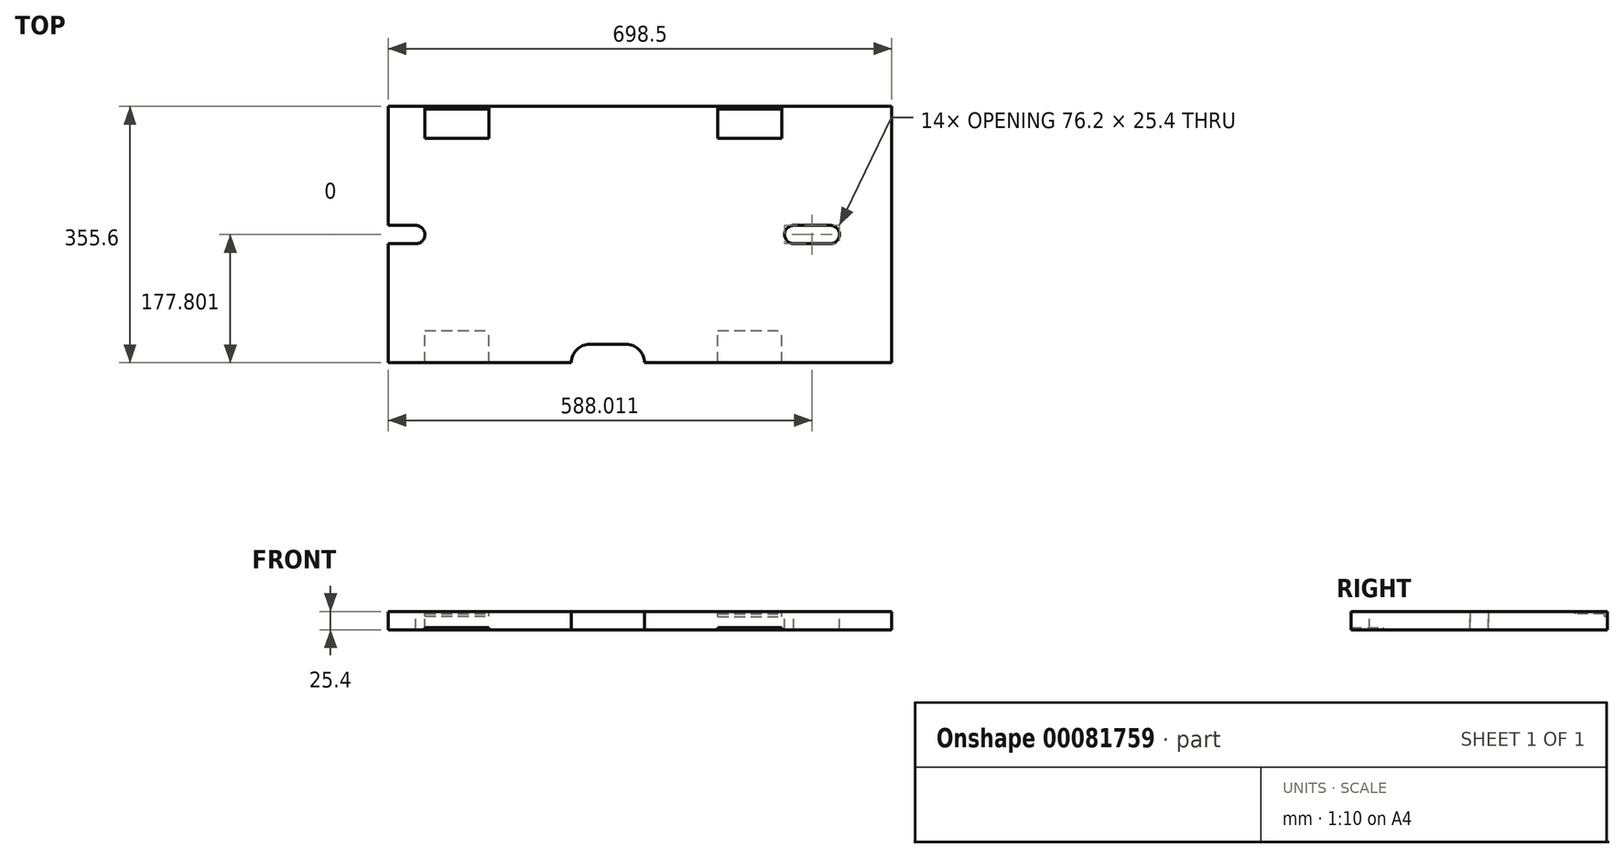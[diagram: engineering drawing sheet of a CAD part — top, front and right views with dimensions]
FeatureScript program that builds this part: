
annotation { "Feature Type Name" : "Feature", "Feature Type Description" : "" }
export const myFeature = defineFeature(function(context is Context, id is Id, definition is map)
    precondition{}
    {
        {
            var Q0;
            Q0=qCreatedBy(makeId("Top.planeOp"),FACE);
            var sketch = newSketch(context, id + "F0", { "sketchPlane" : qUnion([Q0])});
            skLineSegment(sketch, "E0.bottom", {"start": v(-349.25, -177.8) * mm, "end": v(349.25, -177.8) * mm});
            skLineSegment(sketch, "E0.top", {"start": v(-349.25, 177.8) * mm, "end": v(349.25, 177.8) * mm});
            skLineSegment(sketch, "E0.left", {"start": v(-349.25, -177.8) * mm, "end": v(-349.25, 177.8) * mm});
            skLineSegment(sketch, "E0.right", {"start": v(349.25, -177.8) * mm, "end": v(349.25, 177.8) * mm});
            skPoint(sketch, "E0.middle", {"position": v(0, 0) * mm});
            skSolve(sketch);
        }
        {
            var Q0;
            Q0=makeQuery(id+"F0.imprint","IMPRINT",FACE,{"disambiguationData":[TD([[makeQuery(id+"F0.imprint","IMPRINT",EDGE,{"derivedFrom":sQuery(id+"F0.wireOp",EDGE,"E0.bottom")}),1.0]])]});
            extrude(context, id + "F1", {"entities" : qUnion([Q0]), "depth" : 25.4 * mm});
        }
        {
            var Q0;
            Q0=makeQuery(id+"F1.opExtrude","CAP_FACE",FACE,{"disambiguationData":[OSD([sQuery(id+"F0.wireOp",EDGE,"E0.bottom"),sQuery(id+"F0.wireOp",EDGE,"E0.top"),sQuery(id+"F0.wireOp",EDGE,"E0.left"),sQuery(id+"F0.wireOp",EDGE,"E0.right")])],"isStart":false});
            var sketch = newSketch(context, id + "F2", { "sketchPlane" : qUnion([Q0])});
            skLineSegment(sketch, "E1.bottom", {"start": v(-298.45, 177.8) * mm, "end": v(-209.55, 177.8) * mm});
            skLineSegment(sketch, "E1.top", {"start": v(-298.45, 133.35) * mm, "end": v(-209.55, 133.35) * mm});
            skLineSegment(sketch, "E1.left", {"start": v(-298.45, 177.8) * mm, "end": v(-298.45, 133.35) * mm});
            skLineSegment(sketch, "E1.right", {"start": v(-209.55, 177.8) * mm, "end": v(-209.55, 133.35) * mm});
            skLineSegment(sketch, "E2.bottom", {"start": v(107.95, 177.8) * mm, "end": v(196.85, 177.8) * mm});
            skLineSegment(sketch, "E2.top", {"start": v(107.95, 133.35) * mm, "end": v(196.85, 133.35) * mm});
            skLineSegment(sketch, "E2.left", {"start": v(107.95, 177.8) * mm, "end": v(107.95, 133.35) * mm});
            skLineSegment(sketch, "E2.right", {"start": v(196.85, 177.8) * mm, "end": v(196.85, 133.35) * mm});
            skSolve(sketch);
        }
        {
            var Q0;
            Q0 = qSketchRegion(id + "F2", true);
            extrude(context, id + "F3", {"entities" : qUnion([Q0]), "operationType" : NewBodyOperationType.REMOVE, "oppositeDirection" : true, "depth" : 3.17 * mm});
        }
        {
            var Q0;
            Q0=makeQuery(id+"F1.opExtrude","CAP_FACE",FACE,{"disambiguationData":[OSD([sQuery(id+"F0.wireOp",EDGE,"E0.bottom"),sQuery(id+"F0.wireOp",EDGE,"E0.top"),sQuery(id+"F0.wireOp",EDGE,"E0.left"),sQuery(id+"F0.wireOp",EDGE,"E0.right")])],"isStart":true});
            var sketch = newSketch(context, id + "F4", { "sketchPlane" : qUnion([Q0])});
            skLineSegment(sketch, "E3.bottom", {"start": v(-298.45, 177.8) * mm, "end": v(-209.55, 177.8) * mm});
            skLineSegment(sketch, "E3.top", {"start": v(-298.45, 133.35) * mm, "end": v(-209.55, 133.35) * mm});
            skLineSegment(sketch, "E3.left", {"start": v(-298.45, 177.8) * mm, "end": v(-298.45, 133.35) * mm});
            skLineSegment(sketch, "E3.right", {"start": v(-209.55, 177.8) * mm, "end": v(-209.55, 133.35) * mm});
            skLineSegment(sketch, "E4.bottom", {"start": v(107.95, 177.8) * mm, "end": v(196.85, 177.8) * mm});
            skLineSegment(sketch, "E4.top", {"start": v(107.95, 133.35) * mm, "end": v(196.85, 133.35) * mm});
            skLineSegment(sketch, "E4.left", {"start": v(107.95, 177.8) * mm, "end": v(107.95, 133.35) * mm});
            skLineSegment(sketch, "E4.right", {"start": v(196.85, 177.8) * mm, "end": v(196.85, 133.35) * mm});
            skSolve(sketch);
        }
        {
            var Q0;
            Q0 = qSketchRegion(id + "F4", true);
            extrude(context, id + "F5", {"entities" : qUnion([Q0]), "operationType" : NewBodyOperationType.REMOVE, "oppositeDirection" : true, "depth" : 3.17 * mm});
        }
        {
            var Q0;
            Q0=makeQuery(id+"F3.boolean.opBoolean","COPY",FACE,{"derivedFrom":makeQuery(id+"F3.opExtrude","CAP_FACE",FACE,{"disambiguationData":[OSD([sQuery(id+"F2.wireOp",EDGE,"E1.bottom"),sQuery(id+"F2.wireOp",EDGE,"E1.top"),sQuery(id+"F2.wireOp",EDGE,"E1.left"),sQuery(id+"F2.wireOp",EDGE,"E1.right")])],"isStart":false})});
            var sketch = newSketch(context, id + "F6", { "sketchPlane" : qUnion([Q0])});
            skLineSegment(sketch, "E5.bottom", {"start": v(-298.45, 177.8) * mm, "end": v(-209.55, 177.8) * mm});
            skLineSegment(sketch, "E5.top", {"start": v(-298.45, 174) * mm, "end": v(-209.55, 174) * mm});
            skLineSegment(sketch, "E5.left", {"start": v(-298.45, 177.8) * mm, "end": v(-298.45, 174) * mm});
            skLineSegment(sketch, "E5.right", {"start": v(-209.55, 177.8) * mm, "end": v(-209.55, 174) * mm});
            skSolve(sketch);
        }
        {
            var Q0;
            Q0 = qSketchRegion(id + "F6", true);
            extrude(context, id + "F7", {"entities" : qUnion([Q0]), "operationType" : NewBodyOperationType.REMOVE, "oppositeDirection" : true, "depth" : 3.17 * mm});
        }
        {
            var Q0;
            Q0=makeQuery(id+"F3.boolean.opBoolean","COPY",FACE,{"derivedFrom":makeQuery(id+"F3.opExtrude","CAP_FACE",FACE,{"disambiguationData":[OSD([sQuery(id+"F2.wireOp",EDGE,"E2.bottom"),sQuery(id+"F2.wireOp",EDGE,"E2.top"),sQuery(id+"F2.wireOp",EDGE,"E2.left"),sQuery(id+"F2.wireOp",EDGE,"E2.right")])],"isStart":false})});
            var sketch = newSketch(context, id + "F8", { "sketchPlane" : qUnion([Q0])});
            skLineSegment(sketch, "E6.bottom", {"start": v(107.95, 177.8) * mm, "end": v(196.85, 177.8) * mm});
            skLineSegment(sketch, "E6.top", {"start": v(107.95, 174) * mm, "end": v(196.85, 174) * mm});
            skLineSegment(sketch, "E6.left", {"start": v(107.95, 177.8) * mm, "end": v(107.95, 174) * mm});
            skLineSegment(sketch, "E6.right", {"start": v(196.85, 177.8) * mm, "end": v(196.85, 174) * mm});
            skSolve(sketch);
        }
        {
            var Q0;
            Q0 = qSketchRegion(id + "F8", true);
            extrude(context, id + "F9", {"entities" : qUnion([Q0]), "operationType" : NewBodyOperationType.REMOVE, "oppositeDirection" : true, "depth" : 3.8 * mm});
        }
        {
            var Q0;
            Q0=makeQuery(id+"F1.opExtrude","CAP_FACE",FACE,{"disambiguationData":[OSD([sQuery(id+"F0.wireOp",EDGE,"E0.bottom"),sQuery(id+"F0.wireOp",EDGE,"E0.top"),sQuery(id+"F0.wireOp",EDGE,"E0.left"),sQuery(id+"F0.wireOp",EDGE,"E0.right")])],"isStart":false});
            var sketch = newSketch(context, id + "F10", { "sketchPlane" : qUnion([Q0])});
            skArc(sketch, "E7", {"start": v(-311, -12.7) * mm, "mid": v(-298.45, 0.15) * mm, "end": v(-311.3, 12.7) * mm});
            skLineSegment(sketch, "E8.bottom", {"start": v(-311, 12.7) * mm, "end": v(-354.88, 12.7) * mm});
            skLineSegment(sketch, "E8.top", {"start": v(-311, -12.7) * mm, "end": v(-354.88, -12.7) * mm});
            skLineSegment(sketch, "E8.left", {"start": v(-311, -12.7) * mm, "end": v(-311, -12.7) * mm});
            skLineSegment(sketch, "E8.right", {"start": v(-354.88, 12.7) * mm, "end": v(-354.88, -12.7) * mm});
            skArc(sketch, "E9", {"start": v(213.18, 12.7) * mm, "mid": v(200.66, -0.18) * mm, "end": v(213.54, -12.7) * mm});
            skLineSegment(sketch, "E10.bottom", {"start": v(213.18, -12.7) * mm, "end": v(264.16, -12.7) * mm});
            skLineSegment(sketch, "E10.top", {"start": v(213.18, 12.7) * mm, "end": v(264.16, 12.7) * mm});
            skLineSegment(sketch, "E10.left", {"start": v(213.18, 12.7) * mm, "end": v(213.18, 12.7) * mm});
            skArc(sketch, "E11", {"start": v(264.16, -12.7) * mm, "mid": v(276.86, 0) * mm, "end": v(264.16, 12.7) * mm});
            skSolve(sketch);
        }
        {
            var Q0;
            Q0 = qSketchRegion(id + "F10", true);
            extrude(context, id + "F11", {"entities" : qUnion([Q0]), "operationType" : NewBodyOperationType.REMOVE, "oppositeDirection" : true, "depth" : 25.4 * mm});
        }
        {
            var Q0;
            Q0=makeQuery(id+"F1.opExtrude","CAP_FACE",FACE,{"disambiguationData":[OSD([sQuery(id+"F0.wireOp",EDGE,"E0.bottom"),sQuery(id+"F0.wireOp",EDGE,"E0.top"),sQuery(id+"F0.wireOp",EDGE,"E0.left"),sQuery(id+"F0.wireOp",EDGE,"E0.right")])],"isStart":false});
            var sketch = newSketch(context, id + "F12", { "sketchPlane" : qUnion([Q0])});
            skLineSegment(sketch, "E12.bottom", {"start": v(-95.25, -177.8) * mm, "end": v(6.35, -177.8) * mm});
            skLineSegment(sketch, "E12.top", {"start": v(-95.25, -152.4) * mm, "end": v(6.35, -152.4) * mm});
            skLineSegment(sketch, "E12.left", {"start": v(-95.25, -177.8) * mm, "end": v(-95.25, -152.4) * mm});
            skLineSegment(sketch, "E12.right", {"start": v(6.35, -177.8) * mm, "end": v(6.35, -152.4) * mm});
            skSolve(sketch);
        }
        {
            var Q0;
            Q0 = qSketchRegion(id + "F12", true);
            extrude(context, id + "F13", {"entities" : qUnion([Q0]), "operationType" : NewBodyOperationType.REMOVE, "oppositeDirection" : true, "depth" : 25.4 * mm});
        }
        {
            var Q0;
            Q0=makeQuery(id+"F13.boolean.opBoolean","COPY",EDGE,{"derivedFrom":makeQuery(id+"F13.opExtrude","SWEPT_EDGE",EDGE,{"disambiguationData":[OSD([sQuery(id+"F12.wireOp",EDGE,"E12.top"),sQuery(id+"F12.wireOp",EDGE,"E12.left")])]})});
            var Q1;
            Q1=makeQuery(id+"F13.boolean.opBoolean","COPY",EDGE,{"derivedFrom":makeQuery(id+"F13.opExtrude","SWEPT_EDGE",EDGE,{"disambiguationData":[OSD([sQuery(id+"F12.wireOp",EDGE,"E12.top"),sQuery(id+"F12.wireOp",EDGE,"E12.right")])]})});
            fillet(context, id + "F14", {"entities" : qUnion([Q0, Q1]), "radius" : 25.4 * mm, "tangentPropagation" : true, "allowEdgeOverflow" : false});
        }
    });
